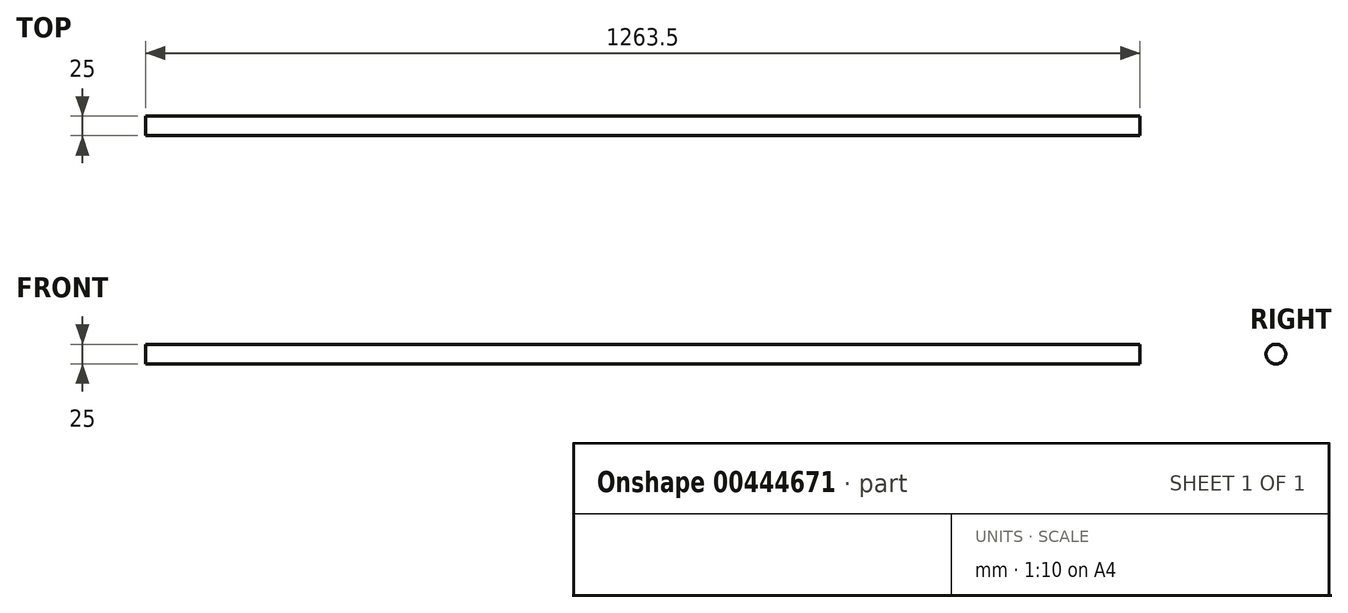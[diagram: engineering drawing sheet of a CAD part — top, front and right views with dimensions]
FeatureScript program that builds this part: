
annotation { "Feature Type Name" : "Feature", "Feature Type Description" : "" }
export const myFeature = defineFeature(function(context is Context, id is Id, definition is map)
    precondition{}
    {
        {
            var Q0;
            Q0=qCreatedBy(makeId("Right.planeOp"),FACE);
            var sketch = newSketch(context, id + "F0", { "sketchPlane" : qUnion([Q0])});
            skCircle(sketch, "E0", {"center": v(37, 7.87) * mm, "radius": 12.5 * mm});
            skSolve(sketch);
        }
        {
            var Q0;
            Q0 = qSketchRegion(id + "F0", true);
            extrude(context, id + "F1", {"entities" : qUnion([Q0]), "depth" : 1263.5 * mm});
        }
    });
